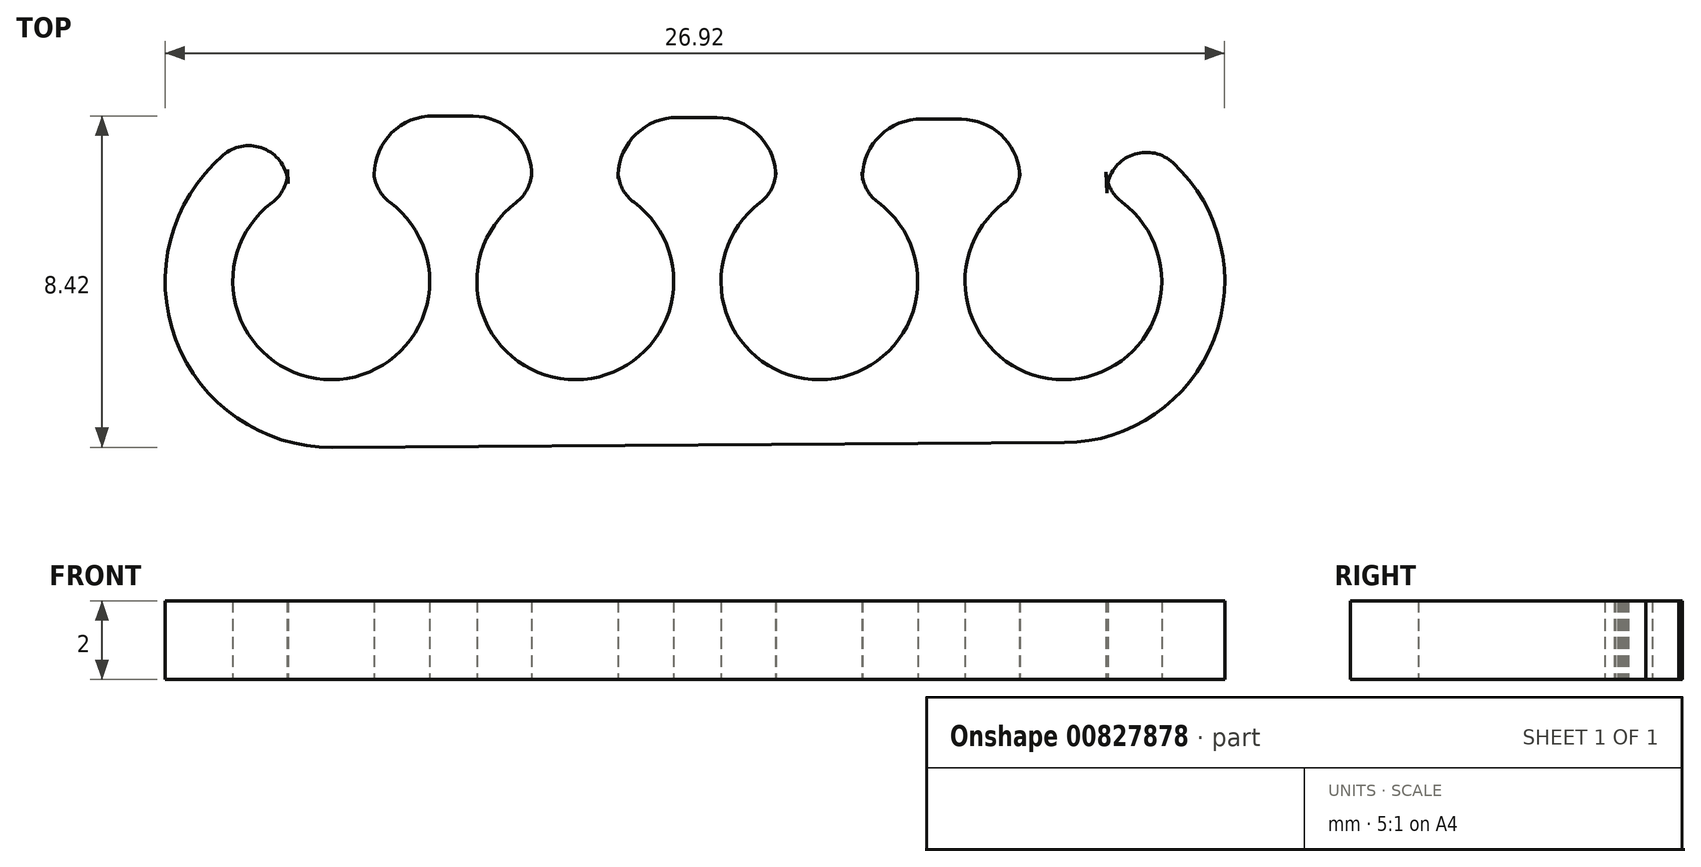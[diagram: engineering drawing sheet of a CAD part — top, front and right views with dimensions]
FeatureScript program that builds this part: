
annotation { "Feature Type Name" : "Feature", "Feature Type Description" : "" }
export const myFeature = defineFeature(function(context is Context, id is Id, definition is map)
    precondition{}
    {
        {
            var Q0;
            Q0=qCreatedBy(makeId("Top.planeOp"),FACE);
            var sketch = newSketch(context, id + "F0", { "sketchPlane" : qUnion([Q0])});
            skArc(sketch, "E0", {"start": v(-23.35, 2) * mm, "mid": v(-21.84, -2.5) * mm, "end": v(-20.36, 2) * mm});
            skArc(sketch, "E1.1.0.0", {"start": v(-17.15, 2) * mm, "mid": v(-15.64, -2.5) * mm, "end": v(-14.16, 2) * mm});
            skArc(sketch, "E1.2.0.0", {"start": v(-10.95, 2) * mm, "mid": v(-9.44, -2.5) * mm, "end": v(-7.96, 2) * mm});
            skArc(sketch, "E1.3.0.0", {"start": v(-4.75, 2) * mm, "mid": v(-3.24, -2.5) * mm, "end": v(-1.76, 2) * mm});
            skLineSegment(sketch, "E1.direction1", {"start": v(-21.85, 0) * mm, "end": v(-15.65, 0) * mm, "construction": true});
            skArc(sketch, "E2", {"start": v(-3.22, -4.1) * mm, "mid": v(0.58, -1.48) * mm, "end": v(-0.46, 3.01) * mm});
            skArc(sketch, "E3", {"start": v(-24.6, 3.2) * mm, "mid": v(-25.8, -1.48) * mm, "end": v(-21.82, -4.22) * mm});
            skLineSegment(sketch, "E4", {"start": v(-21.82, -4.22) * mm, "end": v(-3.22, -4.1) * mm});
            skLineSegment(sketch, "E5", {"start": v(-19.25, 4.2) * mm, "end": v(-18.24, 4.2) * mm});
            skLineSegment(sketch, "E6.bottom", {"start": v(-20.65, 0) * mm, "end": v(-22.85, 0) * mm});
            skLineSegment(sketch, "E6.left", {"start": v(-20.76, 2.65) * mm, "end": v(-20.76, 2.77) * mm});
            skLineSegment(sketch, "E6.right", {"start": v(-22.94, 2.48) * mm, "end": v(-22.96, 2.83) * mm});
            skLineSegment(sketch, "E7.1.0.1", {"start": v(-16.75, 2.75) * mm, "end": v(-16.76, 2.83) * mm});
            skLineSegment(sketch, "E7.1.0.2", {"start": v(-14.56, 2.6) * mm, "end": v(-14.56, 2.77) * mm});
            skLineSegment(sketch, "E7.1.0.3", {"start": v(-14.45, 0) * mm, "end": v(-16.65, 0) * mm});
            skLineSegment(sketch, "E7.2.0.1", {"start": v(-10.55, 2.71) * mm, "end": v(-10.56, 2.83) * mm});
            skLineSegment(sketch, "E7.2.0.2", {"start": v(-8.35, 2.57) * mm, "end": v(-8.36, 2.77) * mm});
            skLineSegment(sketch, "E7.2.0.3", {"start": v(-8.25, 0) * mm, "end": v(-10.45, 0) * mm});
            skLineSegment(sketch, "E7.3.0.1", {"start": v(-4.35, 2.67) * mm, "end": v(-4.36, 2.83) * mm});
            skLineSegment(sketch, "E7.3.0.2", {"start": v(-2.14, 2.24) * mm, "end": v(-2.16, 2.77) * mm});
            skLineSegment(sketch, "E7.3.0.3", {"start": v(-2.05, 0) * mm, "end": v(-4.25, 0) * mm});
            skLineSegment(sketch, "E7.direction1", {"start": v(-22.85, 0) * mm, "end": v(-16.65, 0) * mm, "construction": true});
            skLineSegment(sketch, "E8.trimOffspring", {"start": v(-13.05, 4.16) * mm, "end": v(-12.04, 4.16) * mm});
            skLineSegment(sketch, "E9.trimOffspring", {"start": v(-6.84, 4.12) * mm, "end": v(-5.84, 4.12) * mm});
            skPoint(sketch, "E10.visualSharp", {"position": v(-22.93, 2.25) * mm});
            skArc(sketch, "E10.filletArc", {"start": v(-23.35, 2) * mm, "mid": v(-23.05, 2.36) * mm, "end": v(-22.96, 2.83) * mm});
            skPoint(sketch, "E11.visualSharp", {"position": v(-20.74, 2.24) * mm});
            skArc(sketch, "E11.filletArc", {"start": v(-20.76, 2.77) * mm, "mid": v(-20.65, 2.34) * mm, "end": v(-20.36, 2) * mm});
            skPoint(sketch, "E12.visualSharp", {"position": v(-14.54, 2.24) * mm});
            skArc(sketch, "E12.filletArc", {"start": v(-14.56, 2.77) * mm, "mid": v(-14.45, 2.34) * mm, "end": v(-14.16, 2) * mm});
            skPoint(sketch, "E13.visualSharp", {"position": v(-16.73, 2.25) * mm});
            skArc(sketch, "E13.filletArc", {"start": v(-17.15, 2) * mm, "mid": v(-16.85, 2.36) * mm, "end": v(-16.76, 2.83) * mm});
            skPoint(sketch, "E14.visualSharp", {"position": v(-23, 4.06) * mm});
            skArc(sketch, "E14.filletArc", {"start": v(-22.94, 2.48) * mm, "mid": v(-23.54, 3.36) * mm, "end": v(-24.6, 3.2) * mm});
            skPoint(sketch, "E15.visualSharp", {"position": v(-8.34, 2.24) * mm});
            skArc(sketch, "E15.filletArc", {"start": v(-8.36, 2.77) * mm, "mid": v(-8.25, 2.34) * mm, "end": v(-7.96, 2) * mm});
            skPoint(sketch, "E16.visualSharp", {"position": v(-2.2, 3.97) * mm});
            skArc(sketch, "E16.filletArc", {"start": v(-0.46, 3.01) * mm, "mid": v(-1.56, 3.18) * mm, "end": v(-2.14, 2.24) * mm});
            skPoint(sketch, "E17.visualSharp", {"position": v(-2.14, 2.24) * mm});
            skArc(sketch, "E17.filletArc", {"start": v(-2.16, 2.77) * mm, "mid": v(-2.05, 2.34) * mm, "end": v(-1.76, 2) * mm});
            skPoint(sketch, "E18.visualSharp", {"position": v(-4.33, 2.25) * mm});
            skArc(sketch, "E18.filletArc", {"start": v(-4.75, 2) * mm, "mid": v(-4.45, 2.36) * mm, "end": v(-4.36, 2.83) * mm});
            skPoint(sketch, "E19.visualSharp", {"position": v(-10.53, 2.25) * mm});
            skArc(sketch, "E19.filletArc", {"start": v(-10.95, 2) * mm, "mid": v(-10.65, 2.36) * mm, "end": v(-10.56, 2.83) * mm});
            skPoint(sketch, "E20.visualSharp", {"position": v(-14.62, 4.17) * mm});
            skArc(sketch, "E20.filletArc", {"start": v(-13.05, 4.16) * mm, "mid": v(-14.13, 3.7) * mm, "end": v(-14.56, 2.6) * mm});
            skPoint(sketch, "E21.visualSharp", {"position": v(-16.8, 4.19) * mm});
            skArc(sketch, "E21.filletArc", {"start": v(-16.75, 2.75) * mm, "mid": v(-17.2, 3.77) * mm, "end": v(-18.24, 4.2) * mm});
            skPoint(sketch, "E22.visualSharp", {"position": v(-20.82, 4.21) * mm});
            skArc(sketch, "E22.filletArc", {"start": v(-19.25, 4.2) * mm, "mid": v(-20.34, 3.75) * mm, "end": v(-20.76, 2.65) * mm});
            skPoint(sketch, "E23.visualSharp", {"position": v(-10.6, 4.15) * mm});
            skArc(sketch, "E23.filletArc", {"start": v(-10.55, 2.71) * mm, "mid": v(-11, 3.73) * mm, "end": v(-12.04, 4.16) * mm});
            skPoint(sketch, "E24.visualSharp", {"position": v(-8.41, 4.13) * mm});
            skArc(sketch, "E24.filletArc", {"start": v(-6.84, 4.12) * mm, "mid": v(-7.93, 3.67) * mm, "end": v(-8.35, 2.57) * mm});
            skPoint(sketch, "E25.visualSharp", {"position": v(-4.4, 4.1) * mm});
            skArc(sketch, "E25.filletArc", {"start": v(-4.35, 2.67) * mm, "mid": v(-4.8, 3.7) * mm, "end": v(-5.84, 4.12) * mm});
            skSolve(sketch);
        }
        {
            var Q0;
            Q0 = qSketchRegion(id + "F0", true);
            extrude(context, id + "F1", {"entities" : qUnion([Q0]), "depth" : 2 * mm, "offsetDistance" : 25 * mm});
        }
    });
